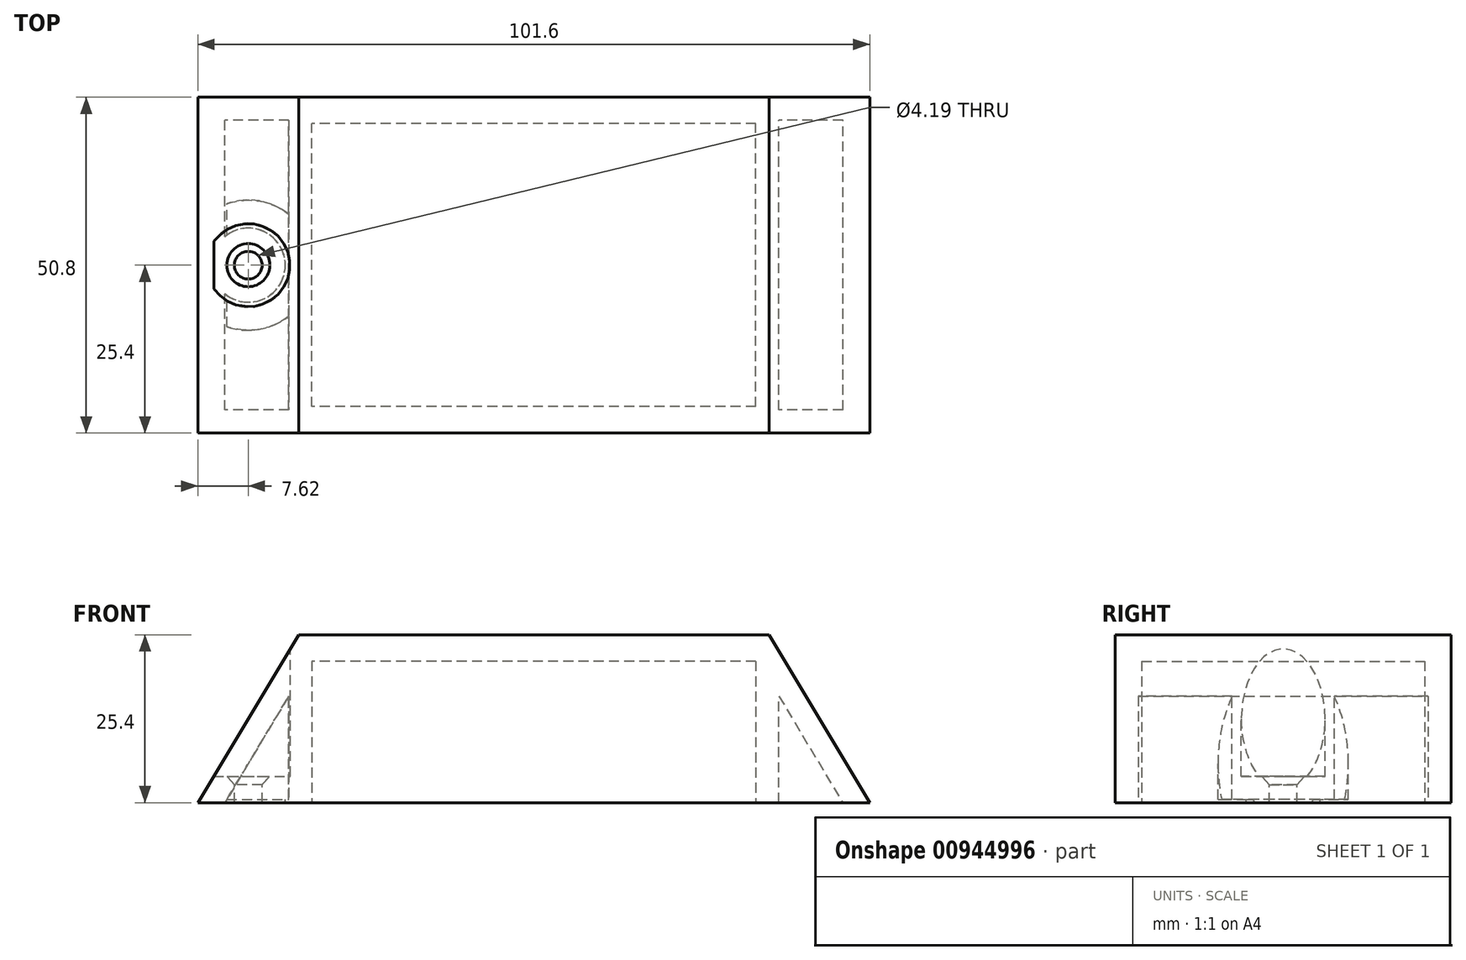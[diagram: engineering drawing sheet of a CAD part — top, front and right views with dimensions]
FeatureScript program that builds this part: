
annotation { "Feature Type Name" : "Feature", "Feature Type Description" : "" }
export const myFeature = defineFeature(function(context is Context, id is Id, definition is map)
    precondition{}
    {
        {
            var Q0;
            Q0=qCreatedBy(makeId("Front.planeOp"),FACE);
            var sketch = newSketch(context, id + "F0", { "sketchPlane" : qUnion([Q0])});
            skLineSegment(sketch, "E0", {"start": v(0, 0) * mm, "end": v(50.8, 0) * mm});
            skLineSegment(sketch, "E1", {"start": v(0, 0) * mm, "end": v(0, 25.4) * mm, "construction": true});
            skLineSegment(sketch, "E2", {"start": v(0, 25.4) * mm, "end": v(35.56, 25.4) * mm});
            skLineSegment(sketch, "E3", {"start": v(35.56, 25.4) * mm, "end": v(50.8, 0) * mm});
            skLineSegment(sketch, "E4.MirrorCS", {"start": v(-35.56, 25.4) * mm, "end": v(-50.8, 0) * mm});
            skLineSegment(sketch, "E5.MirrorCS", {"start": v(0, 25.4) * mm, "end": v(-35.56, 25.4) * mm});
            skLineSegment(sketch, "E6.MirrorCS", {"start": v(0, 0) * mm, "end": v(-50.8, 0) * mm});
            skSolve(sketch);
        }
        {
            var Q0;
            Q0=makeQuery(id+"F0.imprint","IMPRINT",FACE,{"disambiguationData":[TD([[makeQuery(id+"F0.imprint","IMPRINT",EDGE,{"derivedFrom":sQuery(id+"F0.wireOp",EDGE,"E0")}),1.0]])]});
            extrude(context, id + "F1", {"entities" : qUnion([Q0]), "depth" : 25.4 * mm, "offsetDistance" : 25 * mm});
        }
        {
            var Q0;
            Q0=makeQuery(id+"F1.opExtrude","SWEPT_FACE",FACE,{"disambiguationData":[OSD([sQuery(id+"F0.wireOp",EDGE,"E0"),sQuery(id+"F0.wireOp",EDGE,"E6.MirrorCS")])]});
            var sketch = newSketch(context, id + "F2", { "sketchPlane" : qUnion([Q0])});
            skLineSegment(sketch, "E7.0", {"start": v(35.56, 25.4) * mm, "end": v(35.56, 0) * mm});
            skLineSegment(sketch, "E8.0", {"start": v(-35.56, 25.4) * mm, "end": v(-35.56, 0) * mm});
            skLineSegment(sketch, "E9.0", {"start": v(50.8, 25.4) * mm, "end": v(-50.8, 25.4) * mm});
            skLineSegment(sketch, "E10.0", {"start": v(50.8, 21.4) * mm, "end": v(-50.8, 21.4) * mm});
            skLineSegment(sketch, "E11.0", {"start": v(33.56, 25.4) * mm, "end": v(33.56, 0) * mm});
            skLineSegment(sketch, "E12.0", {"start": v(-33.56, 25.4) * mm, "end": v(-33.56, 0) * mm});
            skSolve(sketch);
        }
        {
            var Q0;
            {var subQ0=sQuery(id+"F2.wireOp",EDGE,"E11.0");var subQ1=sQuery(id+"F2.wireOp",EDGE,"E10.0");var subQ2=makeQuery(id+"F2.imprint","INTERSECT",VERTEX,{"derivedFrom":[subQ1,subQ0]});Q0=makeQuery(id+"F2.imprint","IMPRINT",FACE,{"disambiguationData":[TD([[makeQuery(id+"F2.imprint","IMPRINT",EDGE,{"disambiguationData":[TD([[subQ2,-1.0]])],"derivedFrom":subQ1}),1.0]])]});}
            var Q1;
            Q1=makeQuery(id+"F1.opExtrude","SWEPT_FACE",FACE,{"disambiguationData":[OSD([sQuery(id+"F0.wireOp",EDGE,"E2"),sQuery(id+"F0.wireOp",EDGE,"E5.MirrorCS")])]});
            extrude(context, id + "F3", {"entities" : qUnion([Q0]), "operationType" : NewBodyOperationType.REMOVE, "endBound" : BoundingType.UP_TO_SURFACE, "oppositeDirection" : true, "depth" : 25 * mm, "endBoundEntityFace" : qUnion([Q1]), "hasOffset" : true, "offsetDistance" : 4 * mm});
        }
        {
            var Q0;
            Q0=makeQuery(id+"F1.opExtrude","SWEPT_BODY",BODY,{"disambiguationData":[OSD([sQuery(id+"F0.wireOp",EDGE,"E0"),sQuery(id+"F0.wireOp",EDGE,"E2"),sQuery(id+"F0.wireOp",EDGE,"E3"),sQuery(id+"F0.wireOp",EDGE,"E4.MirrorCS"),sQuery(id+"F0.wireOp",EDGE,"E5.MirrorCS"),sQuery(id+"F0.wireOp",EDGE,"E6.MirrorCS")])]});
            var Q1;
            Q1=qCreatedBy(makeId("Front.planeOp"),FACE);
            mirror(context, id + "F4", {"operationType" : NewBodyOperationType.ADD, "entities" : qUnion([Q0]), "mirrorPlane" : qUnion([Q1])});
        }
        {
            var Q0;
            {var subQ0=makeQuery(id+"F1.opExtrude","SWEPT_FACE",FACE,{"disambiguationData":[OSD([sQuery(id+"F0.wireOp",EDGE,"E2"),sQuery(id+"F0.wireOp",EDGE,"E5.MirrorCS")])]});Q0=makeQuery(id+"F4.boolean.opBoolean","MERGE",FACE,{"derivedFrom":[subQ0,makeQuery(id+"F4.opPattern","COPY",FACE,{"derivedFrom":subQ0,"instanceName":"1"})]});}
            var sketch = newSketch(context, id + "F5", { "sketchPlane" : qUnion([Q0])});
            skLineSegment(sketch, "E13.0.0", {"start": v(-35.56, -25.4) * mm, "end": v(-35.56, 25.4) * mm});
            skLineSegment(sketch, "E13.0.1", {"start": v(-35.56, 25.4) * mm, "end": v(-50.8, 25.4) * mm});
            skLineSegment(sketch, "E13.0.2", {"start": v(-50.8, 25.4) * mm, "end": v(-50.8, -25.4) * mm});
            skLineSegment(sketch, "E13.0.3", {"start": v(-50.8, -25.4) * mm, "end": v(-35.56, -25.4) * mm});
            skCircle(sketch, "E14", {"center": v(-43.18, 0) * mm, "radius": 6.35 * mm});
            skPoint(sketch, "E14.centerSnap0", {"position": v(-43.18, 25.4) * mm});
            skSolve(sketch);
        }
        {
            var Q0;
            Q0=makeQuery(id+"F5.imprint","IMPRINT",FACE,{"disambiguationData":[TD([[makeQuery(id+"F5.imprint","IMPRINT",EDGE,{"derivedFrom":sQuery(id+"F5.wireOp",EDGE,"E14")}),1.0]])]});
            var Q1;
            {var subQ0=makeQuery(id+"F1.opExtrude","SWEPT_FACE",FACE,{"disambiguationData":[OSD([sQuery(id+"F0.wireOp",EDGE,"E0"),sQuery(id+"F0.wireOp",EDGE,"E6.MirrorCS")])]});Q1=makeQuery(id+"F4.boolean.opBoolean","MERGE",FACE,{"derivedFrom":[subQ0,makeQuery(id+"F4.opPattern","COPY",FACE,{"derivedFrom":subQ0,"instanceName":"1"})]});}
            extrude(context, id + "F6", {"entities" : qUnion([Q0]), "operationType" : NewBodyOperationType.REMOVE, "endBound" : BoundingType.UP_TO_SURFACE, "oppositeDirection" : true, "depth" : 25 * mm, "endBoundEntityFace" : qUnion([Q1]), "hasOffset" : true, "offsetDistance" : 4 * mm});
        }
        {
            var Q0;
            {var subQ0=makeQuery(id+"F1.opExtrude","SWEPT_FACE",FACE,{"disambiguationData":[OSD([sQuery(id+"F0.wireOp",EDGE,"E2"),sQuery(id+"F0.wireOp",EDGE,"E5.MirrorCS")])]});Q0=makeQuery(id+"F4.boolean.opBoolean","MERGE",FACE,{"derivedFrom":[subQ0,makeQuery(id+"F4.opPattern","COPY",FACE,{"derivedFrom":subQ0,"instanceName":"1"})]});}
            var sketch = newSketch(context, id + "F7", { "sketchPlane" : qUnion([Q0])});
            skArc(sketch, "E15.0", {"start": v(-48.4, 3.62) * mm, "mid": v(-36.83, 0) * mm, "end": v(-48.4, -3.62) * mm});
            skCircle(sketch, "E16", {"center": v(-43.18, 0) * mm, "radius": 2.1 * mm});
            skSolve(sketch);
        }
        {
            var Q0;
            Q0=makeQuery(id+"F7.imprint","IMPRINT",FACE,{"disambiguationData":[TD([[makeQuery(id+"F7.imprint","IMPRINT",EDGE,{"derivedFrom":sQuery(id+"F7.wireOp",EDGE,"E16")}),1.0]])]});
            extrude(context, id + "F8", {"entities" : qUnion([Q0]), "operationType" : NewBodyOperationType.REMOVE, "endBound" : BoundingType.THROUGH_ALL, "oppositeDirection" : true, "depth" : 25 * mm, "offsetDistance" : 25 * mm});
        }
        {
            var Q0;
            Q0=qCreatedBy(makeId("Front.planeOp"),FACE);
            var sketch = newSketch(context, id + "F9", { "sketchPlane" : qUnion([Q0])});
            skLineSegment(sketch, "E17.0", {"start": v(-41.08, 4) * mm, "end": v(-45.28, 4) * mm, "construction": true});
            skLineSegment(sketch, "E18", {"start": v(-43.18, 4) * mm, "end": v(-39.93, 4) * mm});
            skLineSegment(sketch, "E19", {"start": v(-43.18, 4) * mm, "end": v(-43.18, 2) * mm});
            skLineSegment(sketch, "E20", {"start": v(-43.18, 2) * mm, "end": v(-41.76, 2) * mm});
            skLineSegment(sketch, "E21", {"start": v(-41.76, 2) * mm, "end": v(-39.93, 4) * mm});
            skSolve(sketch);
        }
        {
            var Q0;
            Q0=makeQuery(id+"F9.imprint","IMPRINT",FACE,{"disambiguationData":[TD([[makeQuery(id+"F9.imprint","IMPRINT",EDGE,{"derivedFrom":sQuery(id+"F9.wireOp",EDGE,"E18")}),-1.0]])]});
            var Q1;
            Q1=sQuery(id+"F9.wireOp",EDGE,"E19");
            revolve(context, id + "F10", {"operationType" : NewBodyOperationType.REMOVE, "surfaceOperationType" : NewSurfaceOperationType.NEW, "entities" : qUnion([Q0]), "axis" : qUnion([Q1]), "revolveType" : RevolveType.FULL, "oppositeDirection" : true});
        }
        {
            var Q0;
            {var subQ0=makeQuery(id+"F1.opExtrude","SWEPT_FACE",FACE,{"disambiguationData":[OSD([sQuery(id+"F0.wireOp",EDGE,"E0"),sQuery(id+"F0.wireOp",EDGE,"E6.MirrorCS")])]});Q0=makeQuery(id+"F4.boolean.opBoolean","MERGE",FACE,{"derivedFrom":[subQ0,makeQuery(id+"F4.opPattern","COPY",FACE,{"derivedFrom":subQ0,"instanceName":"1"})]});}
            shell(context, id + "F11", {"entities" : qUnion([Q0]), "thickness" : 3.5 * mm});
        }
    });
